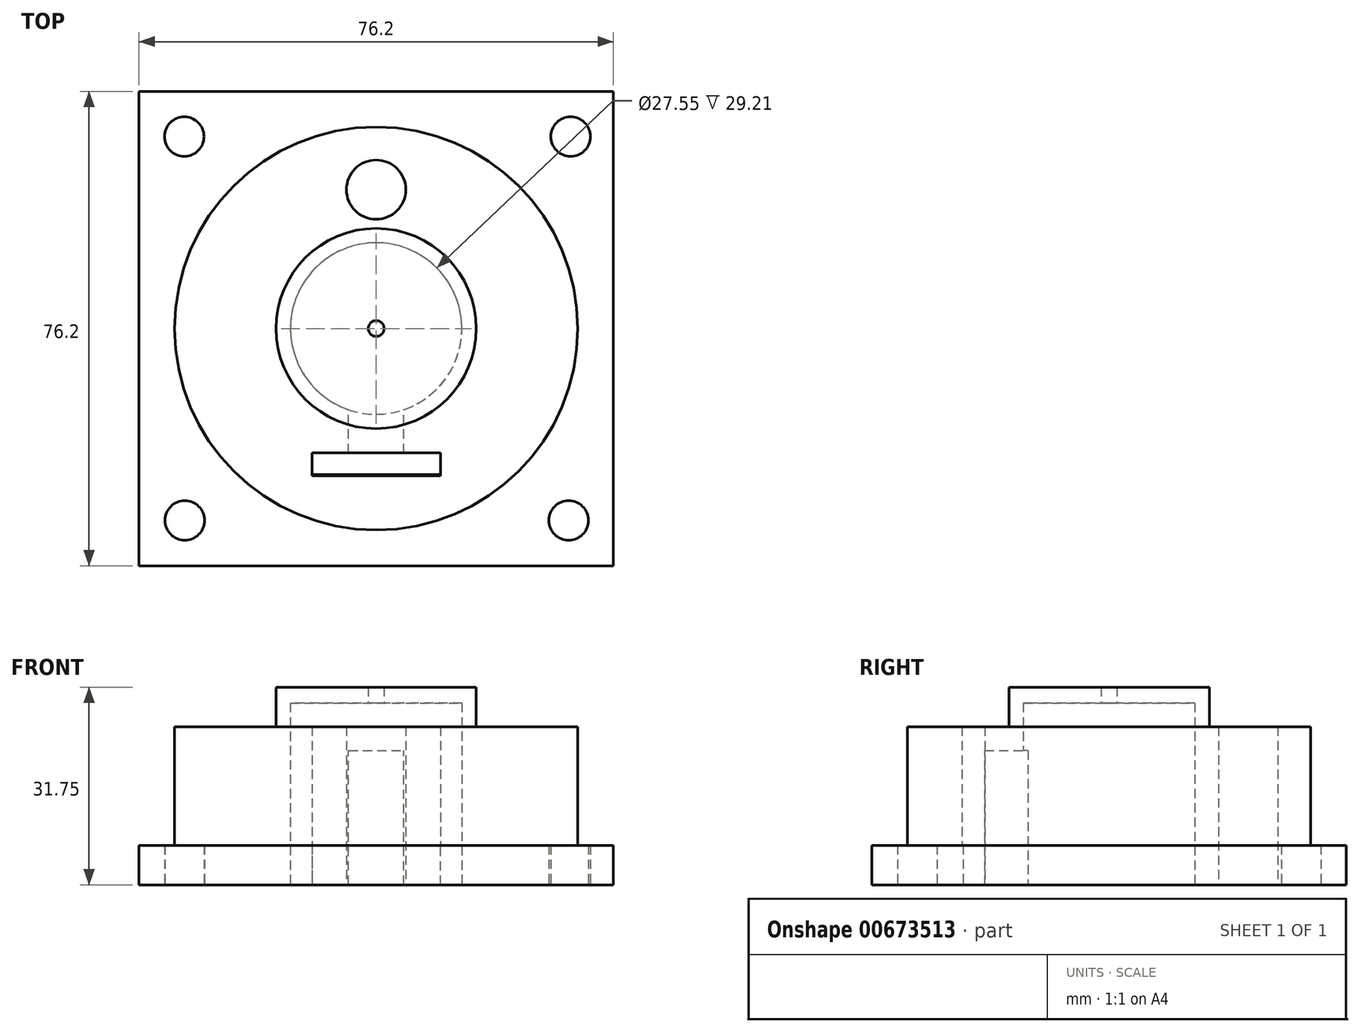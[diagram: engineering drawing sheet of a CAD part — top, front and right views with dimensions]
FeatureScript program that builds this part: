
annotation { "Feature Type Name" : "Feature", "Feature Type Description" : "" }
export const myFeature = defineFeature(function(context is Context, id is Id, definition is map)
    precondition{}
    {
        {
            var Q0;
            Q0=qCreatedBy(makeId("Top.planeOp"),FACE);
            var sketch = newSketch(context, id + "F0", { "sketchPlane" : qUnion([Q0])});
            skLineSegment(sketch, "E0.bottom", {"start": v(-38.1, 38.1) * mm, "end": v(38.1, 38.1) * mm});
            skLineSegment(sketch, "E0.top", {"start": v(-38.1, -38.1) * mm, "end": v(38.1, -38.1) * mm});
            skLineSegment(sketch, "E0.left", {"start": v(-38.1, 38.1) * mm, "end": v(-38.1, -38.1) * mm});
            skLineSegment(sketch, "E0.right", {"start": v(38.1, 38.1) * mm, "end": v(38.1, -38.1) * mm});
            skLineSegment(sketch, "E1", {"start": v(0, 0) * mm, "end": v(0, 38.1) * mm, "construction": true});
            skLineSegment(sketch, "E2", {"start": v(0, 0) * mm, "end": v(0, -38.1) * mm, "construction": true});
            skLineSegment(sketch, "E3", {"start": v(0, 0) * mm, "end": v(-38.1, 0) * mm, "construction": true});
            skLineSegment(sketch, "E4", {"start": v(0, 0) * mm, "end": v(38.1, 0) * mm, "construction": true});
            skPoint(sketch, "E4.endSnap0", {"position": v(38.1, 0) * mm});
            skLineSegment(sketch, "E5", {"start": v(-30.83, 38.1) * mm, "end": v(-30.83, 30.83) * mm, "construction": true});
            skLineSegment(sketch, "E6", {"start": v(-38.1, 30.83) * mm, "end": v(-30.83, 30.83) * mm, "construction": true});
            skLineSegment(sketch, "E7", {"start": v(30.83, 38.1) * mm, "end": v(30.83, 30.83) * mm, "construction": true});
            skLineSegment(sketch, "E8", {"start": v(30.83, 30.83) * mm, "end": v(38.1, 30.83) * mm, "construction": true});
            skLineSegment(sketch, "E9", {"start": v(38.1, 30.83) * mm, "end": v(38.1, 38.1) * mm, "construction": true});
            skLineSegment(sketch, "E10", {"start": v(-38.1, 30.83) * mm, "end": v(-38.1, 38.1) * mm, "construction": true});
            skLineSegment(sketch, "E11", {"start": v(-38.1, -38.1) * mm, "end": v(-38.1, -30.83) * mm, "construction": true});
            skLineSegment(sketch, "E12", {"start": v(-38.1, -30.83) * mm, "end": v(-30.83, -30.83) * mm, "construction": true});
            skLineSegment(sketch, "E13", {"start": v(-30.83, -30.83) * mm, "end": v(-30.83, -38.1) * mm, "construction": true});
            skLineSegment(sketch, "E14", {"start": v(-30.83, -38.1) * mm, "end": v(-38.1, -38.1) * mm, "construction": true});
            skLineSegment(sketch, "E15", {"start": v(38.1, -38.1) * mm, "end": v(38.1, -30.83) * mm, "construction": true});
            skLineSegment(sketch, "E16", {"start": v(38.1, -30.83) * mm, "end": v(30.83, -30.83) * mm, "construction": true});
            skLineSegment(sketch, "E17", {"start": v(30.83, -30.83) * mm, "end": v(30.83, -38.1) * mm, "construction": true});
            skLineSegment(sketch, "E18", {"start": v(30.83, -38.1) * mm, "end": v(38.1, -38.1) * mm, "construction": true});
            skCircle(sketch, "E19", {"center": v(-30.83, 30.83) * mm, "radius": 3.18 * mm});
            skCircle(sketch, "E20", {"center": v(31.24, 30.83) * mm, "radius": 3.18 * mm});
            skCircle(sketch, "E21", {"center": v(30.92, -30.83) * mm, "radius": 3.18 * mm});
            skCircle(sketch, "E22", {"center": v(-30.73, -30.83) * mm, "radius": 3.18 * mm});
            skSolve(sketch);
        }
        {
            var Q0;
            Q0=makeQuery(id+"F0.imprint","IMPRINT",FACE,{"disambiguationData":[TD([[makeQuery(id+"F0.imprint","IMPRINT",EDGE,{"derivedFrom":sQuery(id+"F0.wireOp",EDGE,"E0.bottom")}),-1.0]])]});
            var sketch = newSketch(context, id + "F1", { "sketchPlane" : qUnion([Q0])});
            skCircle(sketch, "E23", {"center": v(0, 0) * mm, "radius": 13.77 * mm});
            skLineSegment(sketch, "E24", {"start": v(0, 0) * mm, "end": v(-13.77, 0) * mm, "construction": true});
            skSolve(sketch);
        }
        {
            var Q0;
            Q0=makeQuery(id+"F0.imprint","IMPRINT",FACE,{"disambiguationData":[TD([[makeQuery(id+"F0.imprint","IMPRINT",EDGE,{"derivedFrom":sQuery(id+"F0.wireOp",EDGE,"E0.bottom")}),-1.0]])]});
            var sketch = newSketch(context, id + "F2", { "sketchPlane" : qUnion([Q0])});
            skCircle(sketch, "E25", {"center": v(0, 0) * mm, "radius": 32.38 * mm});
            skLineSegment(sketch, "E26", {"start": v(0, 0) * mm, "end": v(-32.38, 0) * mm, "construction": true});
            skLineSegment(sketch, "E27", {"start": v(0, 0) * mm, "end": v(13.85, 0) * mm, "construction": true});
            skLineSegment(sketch, "E28.bottom", {"start": v(-12.83, -19.98) * mm, "end": v(13.08, -19.98) * mm});
            skLineSegment(sketch, "E28.top", {"start": v(-12.83, -23.65) * mm, "end": v(13.08, -23.65) * mm});
            skLineSegment(sketch, "E28.left", {"start": v(-12.83, -19.98) * mm, "end": v(-12.83, -23.65) * mm, "construction": true});
            skLineSegment(sketch, "E28.right", {"start": v(13.08, -19.98) * mm, "end": v(13.08, -23.65) * mm, "construction": true});
            skLineSegment(sketch, "E29", {"start": v(-10.3, -19.98) * mm, "end": v(-10.3, -23.65) * mm});
            skLineSegment(sketch, "E30", {"start": v(10.35, -19.98) * mm, "end": v(10.35, -23.65) * mm});
            skLineSegment(sketch, "E31", {"start": v(-10.3, -21.82) * mm, "end": v(10.35, -21.82) * mm, "construction": true});
            skSolve(sketch);
        }
        {
            var Q0;
            Q0=makeQuery(id+"F0.imprint","IMPRINT",FACE,{"disambiguationData":[TD([[makeQuery(id+"F0.imprint","IMPRINT",EDGE,{"derivedFrom":sQuery(id+"F0.wireOp",EDGE,"E0.bottom")}),-1.0]])]});
            var sketch = newSketch(context, id + "F3", { "sketchPlane" : qUnion([Q0])});
            skCircle(sketch, "E32", {"center": v(0, 22.3) * mm, "radius": 5.2 * mm});
            skLineSegment(sketch, "E33", {"start": v(0, 22.3) * mm, "end": v(5.2, 22.3) * mm, "construction": true});
            skSolve(sketch);
        }
        {
            var Q0;
            Q0=makeQuery(id+"F0.imprint","IMPRINT",FACE,{"disambiguationData":[TD([[makeQuery(id+"F0.imprint","IMPRINT",EDGE,{"derivedFrom":sQuery(id+"F0.wireOp",EDGE,"E0.bottom")}),-1.0]])]});
            var sketch = newSketch(context, id + "F4", { "sketchPlane" : qUnion([Q0])});
            skLineSegment(sketch, "E34.bottom", {"start": v(-10.32, -19.85) * mm, "end": v(10.32, -19.85) * mm});
            skLineSegment(sketch, "E34.top", {"start": v(-10.32, -23.48) * mm, "end": v(10.32, -23.48) * mm});
            skLineSegment(sketch, "E34.left", {"start": v(-10.32, -19.85) * mm, "end": v(-10.32, -23.48) * mm});
            skLineSegment(sketch, "E34.right", {"start": v(10.32, -19.85) * mm, "end": v(10.32, -23.48) * mm});
            skLineSegment(sketch, "E35", {"start": v(-10.32, -19.85) * mm, "end": v(0, -19.85) * mm, "construction": true});
            skLineSegment(sketch, "E36", {"start": v(0, -19.85) * mm, "end": v(10.32, -19.85) * mm, "construction": true});
            skLineSegment(sketch, "E37", {"start": v(10.32, -19.85) * mm, "end": v(-10.32, -19.85) * mm});
            skSolve(sketch);
        }
        {
            var Q0;
            Q0 = qSketchRegion(id + "F0", true);
            extrude(context, id + "F5", {"entities" : qUnion([Q0]), "depth" : 6.35 * mm, "offsetDistance" : 25.4 * mm});
        }
        {
            var Q0;
            Q0 = qSketchRegion(id + "F1", true);
            extrude(context, id + "F6", {"entities" : qUnion([Q0]), "operationType" : NewBodyOperationType.REMOVE, "oppositeDirection" : true, "depth" : -25.4 * mm, "offsetDistance" : 25.4 * mm});
        }
        {
            var Q0;
            Q0 = qSketchRegion(id + "F3", true);
            extrude(context, id + "F7", {"entities" : qUnion([Q0]), "operationType" : NewBodyOperationType.REMOVE, "oppositeDirection" : true, "depth" : -25.4 * mm, "offsetDistance" : 25.4 * mm});
        }
        {
            var Q0;
            Q0 = qSketchRegion(id + "F4", true);
            extrude(context, id + "F8", {"entities" : qUnion([Q0]), "operationType" : NewBodyOperationType.REMOVE, "oppositeDirection" : true, "depth" : -25.4 * mm, "offsetDistance" : 25.4 * mm});
        }
        {
            var Q0;
            Q0 = qSketchRegion(id + "F2", true);
            extrude(context, id + "F9", {"entities" : qUnion([Q0]), "operationType" : NewBodyOperationType.ADD, "depth" : 25.4 * mm, "offsetDistance" : 25.4 * mm});
        }
        {
            var Q0;
            Q0=sQuery(id+"F3.wireOp",VERTEX,"E32.center");
            var Q1;
            Q1=makeQuery(id+"F5.opExtrude","SWEPT_BODY",BODY,{"disambiguationData":[OSD([sQuery(id+"F0.wireOp",EDGE,"E0.bottom"),sQuery(id+"F0.wireOp",EDGE,"E0.top"),sQuery(id+"F0.wireOp",EDGE,"E0.left"),sQuery(id+"F0.wireOp",EDGE,"E0.right"),sQuery(id+"F0.wireOp",EDGE,"E19"),sQuery(id+"F0.wireOp",EDGE,"E20"),sQuery(id+"F0.wireOp",EDGE,"E21"),sQuery(id+"F0.wireOp",EDGE,"E22")])]});
            hole(context, id + "F10", {"style" : HoleStyle.SIMPLE, "endStyle" : HoleEndStyle.THROUGH, "oppositeDirection" : true, "holeDiameter" : 9.52 * mm, "majorDiameter" : 6.35 * mm, "isTappedThrough" : true, "tappedDepth" : 12.7 * mm, "tapClearance" : 3, "locations" : qUnion([Q0]), "scope" : qUnion([Q1])});
        }
        {
            var Q0;
            Q0=makeQuery(id+"F9.opExtrude","CAP_FACE",FACE,{"disambiguationData":[OSD([sQuery(id+"F2.wireOp",EDGE,"E25"),sQuery(id+"F2.wireOp",EDGE,"E28.bottom"),sQuery(id+"F2.wireOp",EDGE,"E28.top"),sQuery(id+"F2.wireOp",EDGE,"E28.left"),sQuery(id+"F2.wireOp",EDGE,"E28.right")])],"isStart":false});
            var sketch = newSketch(context, id + "F11", { "sketchPlane" : qUnion([Q0])});
            skCircle(sketch, "E38", {"center": v(0, 0) * mm, "radius": 16.08 * mm});
            skCircle(sketch, "E39", {"center": v(0, 0) * mm, "radius": 1.27 * mm});
            skCircle(sketch, "E40.0", {"center": v(0, 0) * mm, "radius": 13.77 * mm});
            skLineSegment(sketch, "E41", {"start": v(-1.27, 0) * mm, "end": v(1.27, 0) * mm, "construction": true});
            skSolve(sketch);
        }
        {
            var Q0;
            Q0=makeQuery(id+"F11.imprint","IMPRINT",FACE,{"disambiguationData":[TD([[makeQuery(id+"F11.imprint","IMPRINT",EDGE,{"derivedFrom":sQuery(id+"F11.wireOp",EDGE,"E39")}),-1.0]])]});
            var Q1;
            Q1=makeQuery(id+"F11.imprint","IMPRINT",FACE,{"disambiguationData":[TD([[makeQuery(id+"F11.imprint","IMPRINT",EDGE,{"derivedFrom":sQuery(id+"F11.wireOp",EDGE,"E38")}),1.0]])]});
            extrude(context, id + "F12", {"entities" : qUnion([Q0, Q1]), "operationType" : NewBodyOperationType.ADD, "depth" : 6.35 * mm, "offsetDistance" : 25.4 * mm});
        }
        {
            var Q0;
            Q0=makeQuery(id+"F1.imprint","IMPRINT",FACE,{"disambiguationData":[TD([[makeQuery(id+"F1.imprint","IMPRINT",EDGE,{"derivedFrom":sQuery(id+"F1.wireOp",EDGE,"E23")}),1.0]])]});
            var Q1;
            Q1=sQuery(id+"F1.wireOp",EDGE,"E23");
            extrude(context, id + "F13", {"entities" : qUnion([Q0]), "operationType" : NewBodyOperationType.REMOVE, "surfaceEntities" : qUnion([Q1]), "depth" : 29.2 * mm, "offsetDistance" : 25.4 * mm});
        }
        {
            var Q0;
            Q0=makeQuery(id+"F1.imprint","IMPRINT",FACE,{"disambiguationData":[TD([[makeQuery(id+"F1.imprint","IMPRINT",EDGE,{"derivedFrom":sQuery(id+"F1.wireOp",EDGE,"E23")}),-1.0]])]});
            var sketch = newSketch(context, id + "F14", { "sketchPlane" : qUnion([Q0])});
            skLineSegment(sketch, "E42.bottom", {"start": v(-4.44, -20.98) * mm, "end": v(4.45, -20.98) * mm});
            skLineSegment(sketch, "E42.top", {"start": v(-4.45, -12.6) * mm, "end": v(4.44, -12.6) * mm});
            skLineSegment(sketch, "E42.left", {"start": v(-4.45, -20.98) * mm, "end": v(-4.45, -12.6) * mm});
            skLineSegment(sketch, "E42.right", {"start": v(4.45, -20.98) * mm, "end": v(4.45, -12.6) * mm});
            skLineSegment(sketch, "E43", {"start": v(-4.45, -16.79) * mm, "end": v(4.45, -16.79) * mm, "construction": true});
            skLineSegment(sketch, "E44", {"start": v(-4.45, -19.55) * mm, "end": v(0, -19.55) * mm, "construction": true});
            skLineSegment(sketch, "E45", {"start": v(0, -19.55) * mm, "end": v(4.45, -19.55) * mm, "construction": true});
            skSolve(sketch);
        }
        {
            var Q0;
            Q0 = qSketchRegion(id + "F14", true);
            extrude(context, id + "F15", {"entities" : qUnion([Q0]), "operationType" : NewBodyOperationType.REMOVE, "oppositeDirection" : true, "depth" : -21.59 * mm, "offsetDistance" : 25.4 * mm});
        }
    });
